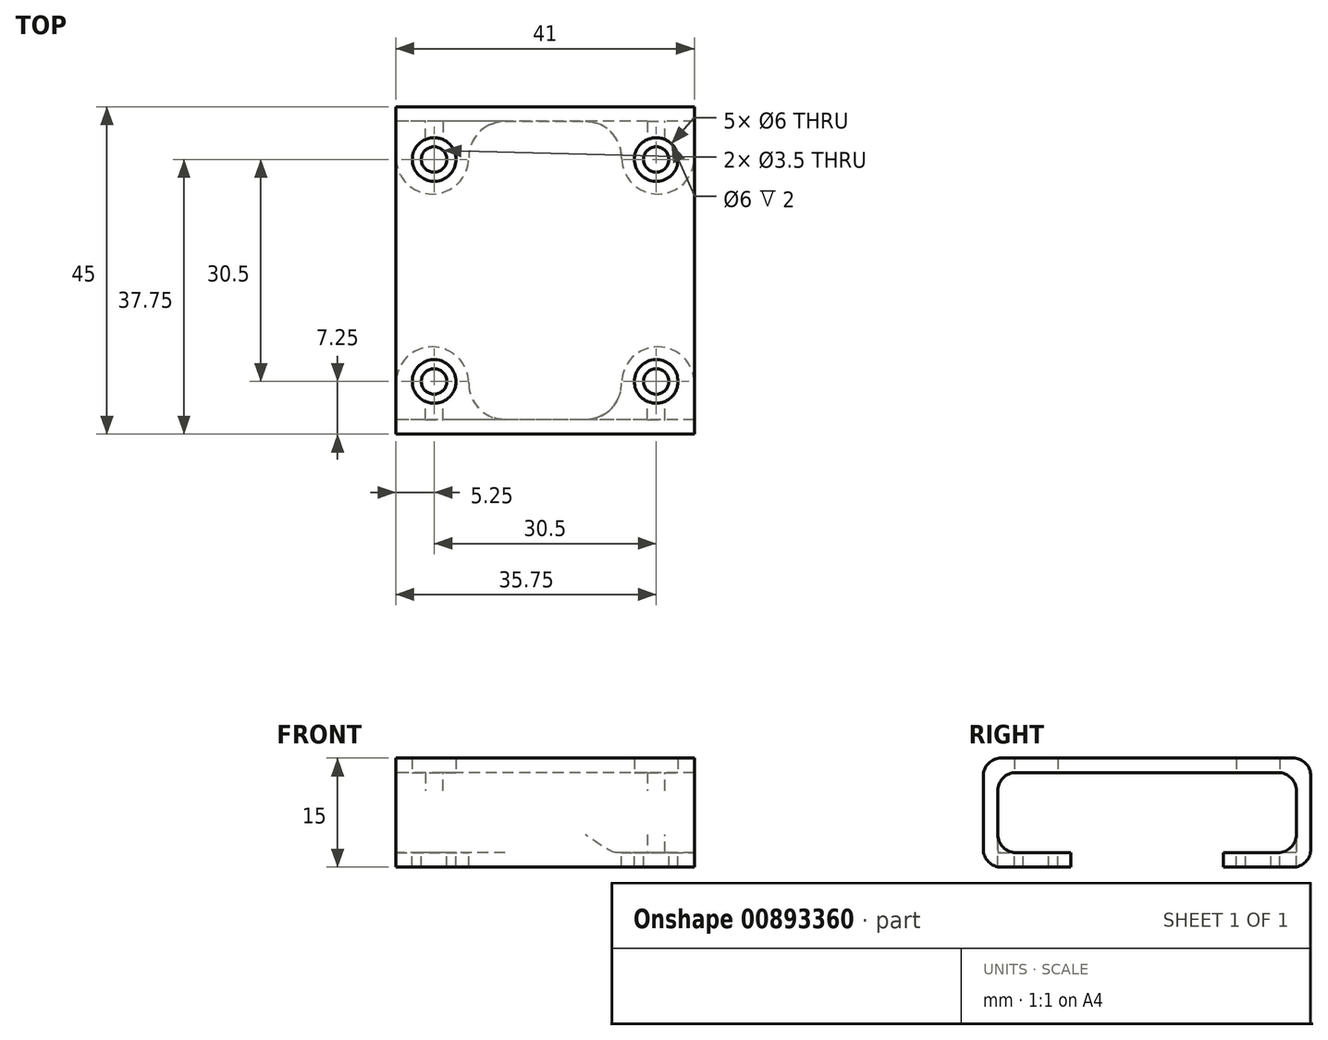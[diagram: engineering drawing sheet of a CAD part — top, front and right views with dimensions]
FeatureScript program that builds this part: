
annotation { "Feature Type Name" : "Feature", "Feature Type Description" : "" }
export const myFeature = defineFeature(function(context is Context, id is Id, definition is map)
    precondition{}
    {
        {
            var Q0;
            Q0=qCreatedBy(makeId("Top.planeOp"),FACE);
            var sketch = newSketch(context, id + "F0", { "sketchPlane" : qUnion([Q0])});
            skPoint(sketch, "E0.middle", {"position": v(0, 0) * mm});
            skLineSegment(sketch, "E1.bottom", {"start": v(15.25, -15.25) * mm, "end": v(-15.25, -15.25) * mm, "construction": true});
            skLineSegment(sketch, "E1.top", {"start": v(15.25, 15.25) * mm, "end": v(-15.25, 15.25) * mm, "construction": true});
            skLineSegment(sketch, "E1.left", {"start": v(15.25, -15.25) * mm, "end": v(15.25, 15.25) * mm, "construction": true});
            skLineSegment(sketch, "E1.right", {"start": v(-15.25, -15.25) * mm, "end": v(-15.25, 15.25) * mm, "construction": true});
            skLineSegment(sketch, "E2", {"start": v(-9.6, 0) * mm, "end": v(8.65, 0) * mm, "construction": true});
            skLineSegment(sketch, "E3", {"start": v(0, 7) * mm, "end": v(0, -6.54) * mm, "construction": true});
            skCircle(sketch, "E4", {"center": v(-15.25, 15.25) * mm, "radius": 1.75 * mm});
            skCircle(sketch, "E5.MirrorC", {"center": v(-15.25, -15.25) * mm, "radius": 1.75 * mm});
            skCircle(sketch, "E6.MirrorC", {"center": v(15.25, 15.25) * mm, "radius": 1.75 * mm});
            skCircle(sketch, "E7.MirrorC", {"center": v(15.25, -15.25) * mm, "radius": 1.75 * mm});
            skLineSegment(sketch, "E8.bottom", {"start": v(22.5, -22.5) * mm, "end": v(-22.5, -22.5) * mm});
            skLineSegment(sketch, "E8.top", {"start": v(22.5, 22.5) * mm, "end": v(-22.5, 22.5) * mm});
            skLineSegment(sketch, "E8.left", {"start": v(22.5, -22.5) * mm, "end": v(22.5, 22.5) * mm});
            skLineSegment(sketch, "E8.right", {"start": v(-22.5, -22.5) * mm, "end": v(-22.5, 22.5) * mm});
            skLineSegment(sketch, "E9.0", {"start": v(20.5, 20.5) * mm, "end": v(-20.5, 20.5) * mm});
            skLineSegment(sketch, "E9.1", {"start": v(20.5, -20.5) * mm, "end": v(20.5, 20.5) * mm});
            skLineSegment(sketch, "E9.2", {"start": v(20.5, -20.5) * mm, "end": v(-20.5, -20.5) * mm});
            skLineSegment(sketch, "E9.3", {"start": v(-20.5, -20.5) * mm, "end": v(-20.5, 20.5) * mm});
            skLineSegment(sketch, "E10.bottom", {"start": v(-20.5, 20.5) * mm, "end": v(-10.5, 20.5) * mm});
            skLineSegment(sketch, "E10.top", {"start": v(-20.5, 10.5) * mm, "end": v(-10.5, 10.5) * mm});
            skLineSegment(sketch, "E10.left", {"start": v(-20.5, 20.5) * mm, "end": v(-20.5, 10.5) * mm});
            skLineSegment(sketch, "E10.right", {"start": v(-10.5, 20.5) * mm, "end": v(-10.5, 10.5) * mm});
            skLineSegment(sketch, "E11.bottom", {"start": v(-20.5, -20.5) * mm, "end": v(-10.5, -20.5) * mm});
            skLineSegment(sketch, "E11.top", {"start": v(-20.5, -10.5) * mm, "end": v(-10.5, -10.5) * mm});
            skLineSegment(sketch, "E11.left", {"start": v(-20.5, -20.5) * mm, "end": v(-20.5, -10.5) * mm});
            skLineSegment(sketch, "E11.right", {"start": v(-10.5, -20.5) * mm, "end": v(-10.5, -10.5) * mm});
            skLineSegment(sketch, "E12.bottom", {"start": v(20.5, -20.5) * mm, "end": v(10.5, -20.5) * mm});
            skLineSegment(sketch, "E12.top", {"start": v(20.5, -10.5) * mm, "end": v(10.5, -10.5) * mm});
            skLineSegment(sketch, "E12.left", {"start": v(20.5, -20.5) * mm, "end": v(20.5, -10.5) * mm});
            skLineSegment(sketch, "E12.right", {"start": v(10.5, -20.5) * mm, "end": v(10.5, -10.5) * mm});
            skLineSegment(sketch, "E13.bottom", {"start": v(20.5, 20.5) * mm, "end": v(10.5, 20.5) * mm});
            skLineSegment(sketch, "E13.top", {"start": v(20.5, 10.5) * mm, "end": v(10.5, 10.5) * mm});
            skLineSegment(sketch, "E13.left", {"start": v(20.5, 20.5) * mm, "end": v(20.5, 10.5) * mm});
            skLineSegment(sketch, "E13.right", {"start": v(10.5, 20.5) * mm, "end": v(10.5, 10.5) * mm});
            skLineSegment(sketch, "E14.bottom", {"start": v(-22.5, 22.5) * mm, "end": v(-20.5, 22.5) * mm});
            skLineSegment(sketch, "E14.top", {"start": v(-22.5, 20.5) * mm, "end": v(-20.5, 20.5) * mm});
            skLineSegment(sketch, "E14.left", {"start": v(-22.5, 22.5) * mm, "end": v(-22.5, 20.5) * mm});
            skLineSegment(sketch, "E14.right", {"start": v(-20.5, 22.5) * mm, "end": v(-20.5, 20.5) * mm});
            skLineSegment(sketch, "E15.bottom", {"start": v(-22.5, -22.5) * mm, "end": v(-20.5, -22.5) * mm});
            skLineSegment(sketch, "E15.top", {"start": v(-22.5, -20.5) * mm, "end": v(-20.5, -20.5) * mm});
            skLineSegment(sketch, "E15.left", {"start": v(-22.5, -22.5) * mm, "end": v(-22.5, -20.5) * mm});
            skLineSegment(sketch, "E15.right", {"start": v(-20.5, -22.5) * mm, "end": v(-20.5, -20.5) * mm});
            skLineSegment(sketch, "E16.bottom", {"start": v(22.5, -22.5) * mm, "end": v(20.5, -22.5) * mm});
            skLineSegment(sketch, "E16.top", {"start": v(22.5, -20.5) * mm, "end": v(20.5, -20.5) * mm});
            skLineSegment(sketch, "E16.left", {"start": v(22.5, -22.5) * mm, "end": v(22.5, -20.5) * mm});
            skLineSegment(sketch, "E16.right", {"start": v(20.5, -22.5) * mm, "end": v(20.5, -20.5) * mm});
            skLineSegment(sketch, "E17.bottom", {"start": v(22.5, 22.5) * mm, "end": v(20.5, 22.5) * mm});
            skLineSegment(sketch, "E17.top", {"start": v(22.5, 20.5) * mm, "end": v(20.5, 20.5) * mm});
            skLineSegment(sketch, "E17.left", {"start": v(22.5, 22.5) * mm, "end": v(22.5, 20.5) * mm});
            skLineSegment(sketch, "E17.right", {"start": v(20.5, 22.5) * mm, "end": v(20.5, 20.5) * mm});
            skCircle(sketch, "E18", {"center": v(-15.25, 15.25) * mm, "radius": 3 * mm});
            skCircle(sketch, "E19.MirrorC", {"center": v(-15.25, -15.25) * mm, "radius": 3 * mm});
            skCircle(sketch, "E20.MirrorC", {"center": v(15.25, 15.25) * mm, "radius": 3 * mm});
            skCircle(sketch, "E21.MirrorC", {"center": v(15.25, -15.25) * mm, "radius": 3 * mm});
            skSolve(sketch);
        }
        {
            var Q0;
            Q0=makeQuery(id+"F0.imprint","IMPRINT",FACE,{"disambiguationData":[TD([[makeQuery(id+"F0.imprint","IMPRINT",EDGE,{"derivedFrom":sQuery(id+"F0.wireOp",EDGE,"E4")}),-1.0]])]});
            var Q1;
            Q1=makeQuery(id+"F0.imprint","IMPRINT",FACE,{"disambiguationData":[TD([[makeQuery(id+"F0.imprint","IMPRINT",EDGE,{"derivedFrom":sQuery(id+"F0.wireOp",EDGE,"E6.MirrorC")}),1.0]])]});
            var Q2;
            Q2=makeQuery(id+"F0.imprint","IMPRINT",FACE,{"disambiguationData":[TD([[makeQuery(id+"F0.imprint","IMPRINT",EDGE,{"derivedFrom":sQuery(id+"F0.wireOp",EDGE,"E7.MirrorC")}),-1.0]])]});
            var Q3;
            Q3=makeQuery(id+"F0.imprint","IMPRINT",FACE,{"disambiguationData":[TD([[makeQuery(id+"F0.imprint","IMPRINT",EDGE,{"derivedFrom":sQuery(id+"F0.wireOp",EDGE,"E5.MirrorC")}),1.0]])]});
            var Q4;
            {var subQ4=sQuery(id+"F0.wireOp",EDGE,"E15.right");Q4=makeQuery(id+"F0.imprint","IMPRINT",FACE,{"disambiguationData":[TD([[makeQuery(id+"F0.imprint","IMPRINT",EDGE,{"derivedFrom":subQ4}),-1.0]])]});}
            var Q5;
            {var subQ0=sQuery(id+"F0.wireOp",EDGE,"E14.right");Q5=makeQuery(id+"F0.imprint","IMPRINT",FACE,{"disambiguationData":[TD([[makeQuery(id+"F0.imprint","IMPRINT",EDGE,{"derivedFrom":subQ0}),1.0]])]});}
            var Q6;
            {var subQ4=sQuery(id+"F0.wireOp",EDGE,"E10.top");Q6=makeQuery(id+"F0.imprint","IMPRINT",FACE,{"disambiguationData":[TD([[makeQuery(id+"F0.imprint","IMPRINT",EDGE,{"derivedFrom":subQ4}),1.0]])]});}
            var Q7;
            {var subQ1=sQuery(id+"F0.wireOp",EDGE,"E13.top");Q7=makeQuery(id+"F0.imprint","IMPRINT",FACE,{"disambiguationData":[TD([[makeQuery(id+"F0.imprint","IMPRINT",EDGE,{"derivedFrom":subQ1}),-1.0]])]});}
            var Q8;
            {var subQ0=sQuery(id+"F0.wireOp",EDGE,"E12.top");Q8=makeQuery(id+"F0.imprint","IMPRINT",FACE,{"disambiguationData":[TD([[makeQuery(id+"F0.imprint","IMPRINT",EDGE,{"derivedFrom":subQ0}),1.0]])]});}
            var Q9;
            {var subQ0=sQuery(id+"F0.wireOp",EDGE,"E11.top");Q9=makeQuery(id+"F0.imprint","IMPRINT",FACE,{"disambiguationData":[TD([[makeQuery(id+"F0.imprint","IMPRINT",EDGE,{"derivedFrom":subQ0}),-1.0]])]});}
            extrude(context, id + "F1", {"entities" : qUnion([Q0, Q1, Q2, Q3, Q4, Q5, Q6, Q7, Q8, Q9]), "oppositeDirection" : true, "depth" : 2 * mm, "offsetDistance" : 25 * mm});
        }
        {
            var Q0;
            Q0=makeQuery(id+"F1.opExtrude","SWEPT_EDGE",EDGE,{"disambiguationData":[OSD([sQuery(id+"F0.wireOp",EDGE,"E9.0"),sQuery(id+"F0.wireOp",EDGE,"E10.right")])]});
            var Q1;
            Q1=makeQuery(id+"F1.opExtrude","SWEPT_EDGE",EDGE,{"disambiguationData":[OSD([sQuery(id+"F0.wireOp",EDGE,"E10.top"),sQuery(id+"F0.wireOp",EDGE,"E10.right")])]});
            var Q2;
            Q2=makeQuery(id+"F1.opExtrude","SWEPT_EDGE",EDGE,{"disambiguationData":[OSD([sQuery(id+"F0.wireOp",EDGE,"E9.3"),sQuery(id+"F0.wireOp",EDGE,"E10.top")])]});
            var Q3;
            Q3=makeQuery(id+"F1.opExtrude","SWEPT_EDGE",EDGE,{"disambiguationData":[OSD([sQuery(id+"F0.wireOp",EDGE,"E9.3"),sQuery(id+"F0.wireOp",EDGE,"E11.top")])]});
            var Q4;
            Q4=makeQuery(id+"F1.opExtrude","SWEPT_EDGE",EDGE,{"disambiguationData":[OSD([sQuery(id+"F0.wireOp",EDGE,"E11.top"),sQuery(id+"F0.wireOp",EDGE,"E11.right")])]});
            var Q5;
            Q5=makeQuery(id+"F1.opExtrude","SWEPT_EDGE",EDGE,{"disambiguationData":[OSD([sQuery(id+"F0.wireOp",EDGE,"E9.2"),sQuery(id+"F0.wireOp",EDGE,"E11.right")])]});
            var Q6;
            Q6=makeQuery(id+"F1.opExtrude","SWEPT_EDGE",EDGE,{"disambiguationData":[OSD([sQuery(id+"F0.wireOp",EDGE,"E9.2"),sQuery(id+"F0.wireOp",EDGE,"E12.right")])]});
            var Q7;
            Q7=makeQuery(id+"F1.opExtrude","SWEPT_EDGE",EDGE,{"disambiguationData":[OSD([sQuery(id+"F0.wireOp",EDGE,"E12.top"),sQuery(id+"F0.wireOp",EDGE,"E12.right")])]});
            var Q8;
            Q8=makeQuery(id+"F1.opExtrude","SWEPT_EDGE",EDGE,{"disambiguationData":[OSD([sQuery(id+"F0.wireOp",EDGE,"E9.1"),sQuery(id+"F0.wireOp",EDGE,"E12.top")])]});
            var Q9;
            Q9=makeQuery(id+"F1.opExtrude","SWEPT_EDGE",EDGE,{"disambiguationData":[OSD([sQuery(id+"F0.wireOp",EDGE,"E13.top"),sQuery(id+"F0.wireOp",EDGE,"E13.right")])]});
            var Q10;
            Q10=makeQuery(id+"F1.opExtrude","SWEPT_EDGE",EDGE,{"disambiguationData":[OSD([sQuery(id+"F0.wireOp",EDGE,"E9.0"),sQuery(id+"F0.wireOp",EDGE,"E13.right")])]});
            var Q11;
            Q11=makeQuery(id+"F1.opExtrude","SWEPT_EDGE",EDGE,{"disambiguationData":[OSD([sQuery(id+"F0.wireOp",EDGE,"E9.1"),sQuery(id+"F0.wireOp",EDGE,"E13.top")])]});
            fillet(context, id + "F2", {"entities" : qUnion([Q0, Q1, Q2, Q3, Q4, Q5, Q6, Q7, Q8, Q9, Q10, Q11]), "radius" : 5 * mm, "tangentPropagation" : true, "defaultsChanged" : false, "vertexSettings" : [], "allowEdgeOverflow" : false});
        }
        {
            var Q0;
            {var subQ0=sQuery(id+"F0.wireOp",EDGE,"E14.right");Q0=makeQuery(id+"F0.imprint","IMPRINT",FACE,{"disambiguationData":[TD([[makeQuery(id+"F0.imprint","IMPRINT",EDGE,{"derivedFrom":subQ0}),1.0]])]});}
            var Q1;
            {var subQ4=sQuery(id+"F0.wireOp",EDGE,"E15.right");Q1=makeQuery(id+"F0.imprint","IMPRINT",FACE,{"disambiguationData":[TD([[makeQuery(id+"F0.imprint","IMPRINT",EDGE,{"derivedFrom":subQ4}),-1.0]])]});}
            extrude(context, id + "F3", {"entities" : qUnion([Q0, Q1]), "depth" : 13 * mm, "offsetDistance" : 25 * mm});
        }
        {
            var Q0;
            {var subQ4=sQuery(id+"F0.wireOp",EDGE,"E10.top");Q0=makeQuery(id+"F0.imprint","IMPRINT",FACE,{"disambiguationData":[TD([[makeQuery(id+"F0.imprint","IMPRINT",EDGE,{"derivedFrom":subQ4}),1.0]])]});}
            var Q1;
            {var subQ3=sQuery(id+"F0.wireOp",EDGE,"E10.top");Q1=makeQuery(id+"F0.imprint","IMPRINT",FACE,{"disambiguationData":[TD([[makeQuery(id+"F0.imprint","IMPRINT",EDGE,{"derivedFrom":subQ3}),-1.0]])]});}
            var Q2;
            {var subQ1=sQuery(id+"F0.wireOp",EDGE,"E13.top");Q2=makeQuery(id+"F0.imprint","IMPRINT",FACE,{"disambiguationData":[TD([[makeQuery(id+"F0.imprint","IMPRINT",EDGE,{"derivedFrom":subQ1}),-1.0]])]});}
            var Q3;
            {var subQ0=sQuery(id+"F0.wireOp",EDGE,"E12.top");Q3=makeQuery(id+"F0.imprint","IMPRINT",FACE,{"disambiguationData":[TD([[makeQuery(id+"F0.imprint","IMPRINT",EDGE,{"derivedFrom":subQ0}),1.0]])]});}
            var Q4;
            {var subQ0=sQuery(id+"F0.wireOp",EDGE,"E11.top");Q4=makeQuery(id+"F0.imprint","IMPRINT",FACE,{"disambiguationData":[TD([[makeQuery(id+"F0.imprint","IMPRINT",EDGE,{"derivedFrom":subQ0}),-1.0]])]});}
            extrude(context, id + "F4", {"entities" : qUnion([Q0, Q1, Q2, Q3, Q4]), "depth" : 2 * mm, "offsetDistance" : 25 * mm});
        }
        {
            var Q0;
            Q0=makeQuery(id+"F4.opExtrude","SWEPT_BODY",BODY,{"disambiguationData":[OSD([sQuery(id+"F0.wireOp",EDGE,"E9.0"),sQuery(id+"F0.wireOp",EDGE,"E9.1"),sQuery(id+"F0.wireOp",EDGE,"E9.2"),sQuery(id+"F0.wireOp",EDGE,"E9.3"),sQuery(id+"F0.wireOp",EDGE,"E18"),sQuery(id+"F0.wireOp",EDGE,"E19.MirrorC"),sQuery(id+"F0.wireOp",EDGE,"E20.MirrorC"),sQuery(id+"F0.wireOp",EDGE,"E21.MirrorC")])]});
            var Q1;
            Q1=makeQuery(id+"F3.opExtrude","SWEPT_EDGE",EDGE,{"disambiguationData":[OSD([sQuery(id+"F0.wireOp",EDGE,"E9.0"),sQuery(id+"F0.wireOp",EDGE,"E9.3"),sQuery(id+"F0.wireOp",EDGE,"E14.top"),sQuery(id+"F0.wireOp",EDGE,"E14.right")])]});
            transform(context, id + "F5", {"entities" : qUnion([Q0]), "transformType" : TransformType.TRANSLATION_DISTANCE, "transformDirection" : qUnion([Q1]), "distance" : 11 * mm, "oppositeDirection" : true, "makeCopy" : false});
        }
        {
            var Q0;
            Q0=makeQuery(id+"F1.opExtrude","SWEPT_BODY",BODY,{"disambiguationData":[OSD([sQuery(id+"F0.wireOp",EDGE,"E4"),sQuery(id+"F0.wireOp",EDGE,"E6.MirrorC"),sQuery(id+"F0.wireOp",EDGE,"E8.top"),sQuery(id+"F0.wireOp",EDGE,"E9.0"),sQuery(id+"F0.wireOp",EDGE,"E9.1"),sQuery(id+"F0.wireOp",EDGE,"E9.3"),sQuery(id+"F0.wireOp",EDGE,"E10.top"),sQuery(id+"F0.wireOp",EDGE,"E10.right"),sQuery(id+"F0.wireOp",EDGE,"E13.top"),sQuery(id+"F0.wireOp",EDGE,"E13.right"),sQuery(id+"F0.wireOp",EDGE,"E14.right"),sQuery(id+"F0.wireOp",EDGE,"E17.right")])]});
            var Q1;
            Q1=makeQuery(id+"F1.opExtrude","SWEPT_BODY",BODY,{"disambiguationData":[OSD([sQuery(id+"F0.wireOp",EDGE,"E5.MirrorC"),sQuery(id+"F0.wireOp",EDGE,"E7.MirrorC"),sQuery(id+"F0.wireOp",EDGE,"E8.bottom"),sQuery(id+"F0.wireOp",EDGE,"E9.1"),sQuery(id+"F0.wireOp",EDGE,"E9.2"),sQuery(id+"F0.wireOp",EDGE,"E9.3"),sQuery(id+"F0.wireOp",EDGE,"E11.top"),sQuery(id+"F0.wireOp",EDGE,"E11.right"),sQuery(id+"F0.wireOp",EDGE,"E12.top"),sQuery(id+"F0.wireOp",EDGE,"E12.right"),sQuery(id+"F0.wireOp",EDGE,"E15.right"),sQuery(id+"F0.wireOp",EDGE,"E16.right")])]});
            var Q2;
            Q2=makeQuery(id+"F3.opExtrude","SWEPT_BODY",BODY,{"disambiguationData":[OSD([sQuery(id+"F0.wireOp",EDGE,"E8.bottom"),sQuery(id+"F0.wireOp",EDGE,"E9.2"),sQuery(id+"F0.wireOp",EDGE,"E15.right"),sQuery(id+"F0.wireOp",EDGE,"E16.right")])]});
            var Q3;
            Q3=makeQuery(id+"F4.opExtrude","SWEPT_BODY",BODY,{"disambiguationData":[OSD([sQuery(id+"F0.wireOp",EDGE,"E9.0"),sQuery(id+"F0.wireOp",EDGE,"E9.1"),sQuery(id+"F0.wireOp",EDGE,"E9.2"),sQuery(id+"F0.wireOp",EDGE,"E9.3"),sQuery(id+"F0.wireOp",EDGE,"E18"),sQuery(id+"F0.wireOp",EDGE,"E19.MirrorC"),sQuery(id+"F0.wireOp",EDGE,"E20.MirrorC"),sQuery(id+"F0.wireOp",EDGE,"E21.MirrorC")])]});
            var Q4;
            Q4=makeQuery(id+"F3.opExtrude","SWEPT_BODY",BODY,{"disambiguationData":[OSD([sQuery(id+"F0.wireOp",EDGE,"E8.top"),sQuery(id+"F0.wireOp",EDGE,"E9.0"),sQuery(id+"F0.wireOp",EDGE,"E14.right"),sQuery(id+"F0.wireOp",EDGE,"E17.right")])]});
            booleanBodies(context, id + "F6", {"operationType" : BooleanOperationType.UNION, "tools" : qUnion([Q0, Q1, Q2, Q3, Q4])});
        }
        {
            var Q0;
            Q0=makeQuery(id+"F4.opExtrude","CAP_EDGE",EDGE,{"disambiguationData":[OSD([sQuery(id+"F0.wireOp",EDGE,"E9.2")])],"isStart":true});
            var Q1;
            Q1=makeQuery(id+"F4.opExtrude","CAP_EDGE",EDGE,{"disambiguationData":[OSD([sQuery(id+"F0.wireOp",EDGE,"E9.0")])],"isStart":true});
            var Q2;
            Q2=makeQuery(id+"F3.opExtrude","CAP_EDGE",EDGE,{"disambiguationData":[OSD([sQuery(id+"F0.wireOp",EDGE,"E8.top")])],"isStart":false});
            var Q3;
            Q3=makeQuery(id+"F3.opExtrude","CAP_EDGE",EDGE,{"disambiguationData":[OSD([sQuery(id+"F0.wireOp",EDGE,"E8.bottom")])],"isStart":false});
            var Q4;
            Q4=makeQuery(id+"F1.opExtrude","CAP_EDGE",EDGE,{"disambiguationData":[OSD([sQuery(id+"F0.wireOp",EDGE,"E8.bottom")])],"isStart":false});
            var Q5;
            {var subQ0=sQuery(id+"F0.wireOp",EDGE,"E9.2");var subQ3=sQuery(id+"F0.wireOp",EDGE,"E16.right");Q5=makeQuery(id+"F6.opBoolean","SPLIT",EDGE,{"disambiguationData":[TD([makeQuery(id+"F3.opExtrude","SWEPT_FACE",FACE,{"disambiguationData":[OSD([subQ3])]})])],"derivedFrom":makeQuery(id+"F3.opExtrude","CAP_EDGE",EDGE,{"disambiguationData":[OSD([subQ0])],"isStart":true})});}
            var Q6;
            {var subQ0=sQuery(id+"F0.wireOp",EDGE,"E14.right");var subQ4=sQuery(id+"F0.wireOp",EDGE,"E9.2");Q6=makeQuery(id+"F6.opBoolean","SPLIT",EDGE,{"disambiguationData":[TD([makeQuery(id+"F3.opExtrude","SWEPT_FACE",FACE,{"disambiguationData":[OSD([subQ0])]})])],"derivedFrom":makeQuery(id+"F3.opExtrude","CAP_EDGE",EDGE,{"disambiguationData":[OSD([subQ4])],"isStart":true})});}
            var Q7;
            Q7=makeQuery(id+"F1.opExtrude","CAP_EDGE",EDGE,{"disambiguationData":[OSD([sQuery(id+"F0.wireOp",EDGE,"E8.top")])],"isStart":false});
            var Q8;
            {var subQ2=sQuery(id+"F0.wireOp",EDGE,"E9.0");var subQ3=sQuery(id+"F0.wireOp",EDGE,"E14.right");Q8=makeQuery(id+"F6.opBoolean","SPLIT",EDGE,{"disambiguationData":[TD([makeQuery(id+"F3.opExtrude","SWEPT_FACE",FACE,{"disambiguationData":[OSD([subQ3])]})])],"derivedFrom":makeQuery(id+"F3.opExtrude","CAP_EDGE",EDGE,{"disambiguationData":[OSD([subQ2])],"isStart":true})});}
            var Q9;
            {var subQ3=sQuery(id+"F0.wireOp",EDGE,"E9.0");var subQ4=sQuery(id+"F0.wireOp",EDGE,"E16.right");Q9=makeQuery(id+"F6.opBoolean","SPLIT",EDGE,{"disambiguationData":[TD([makeQuery(id+"F3.opExtrude","SWEPT_FACE",FACE,{"disambiguationData":[OSD([subQ4])]})])],"derivedFrom":makeQuery(id+"F3.opExtrude","CAP_EDGE",EDGE,{"disambiguationData":[OSD([subQ3])],"isStart":true})});}
            fillet(context, id + "F7", {"entities" : qUnion([Q0, Q1, Q2, Q3, Q4, Q5, Q6, Q7, Q8, Q9]), "radius" : 2.5 * mm, "tangentPropagation" : true, "defaultsChanged" : false, "vertexSettings" : [], "allowEdgeOverflow" : false});
        }
    });
